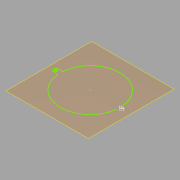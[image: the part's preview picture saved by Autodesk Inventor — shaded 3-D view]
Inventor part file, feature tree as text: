
AUTODESK INVENTOR PART (.ipt)
format: ipt  version: 2015 (Build 190159000, 159)  size: 86,016 bytes
history: native  units: mm
features: plane x1, extrude x1, sketch x1
ambient origin geometry x8: Origin, YZ Plane, XZ Plane, XY Plane, X Axis, Y Axis, Z Axis, Center Point
bodies: Body1 (feature_tree)
feature tree (3):
  plane  "Work Plane1"
  extrude  "Extrusion3"  Depth=36.0mm
  sketch  "Sketch1"  dims[d0=36.0mm d19=36.0mm d26=1.0mm d27=0.0mm]
